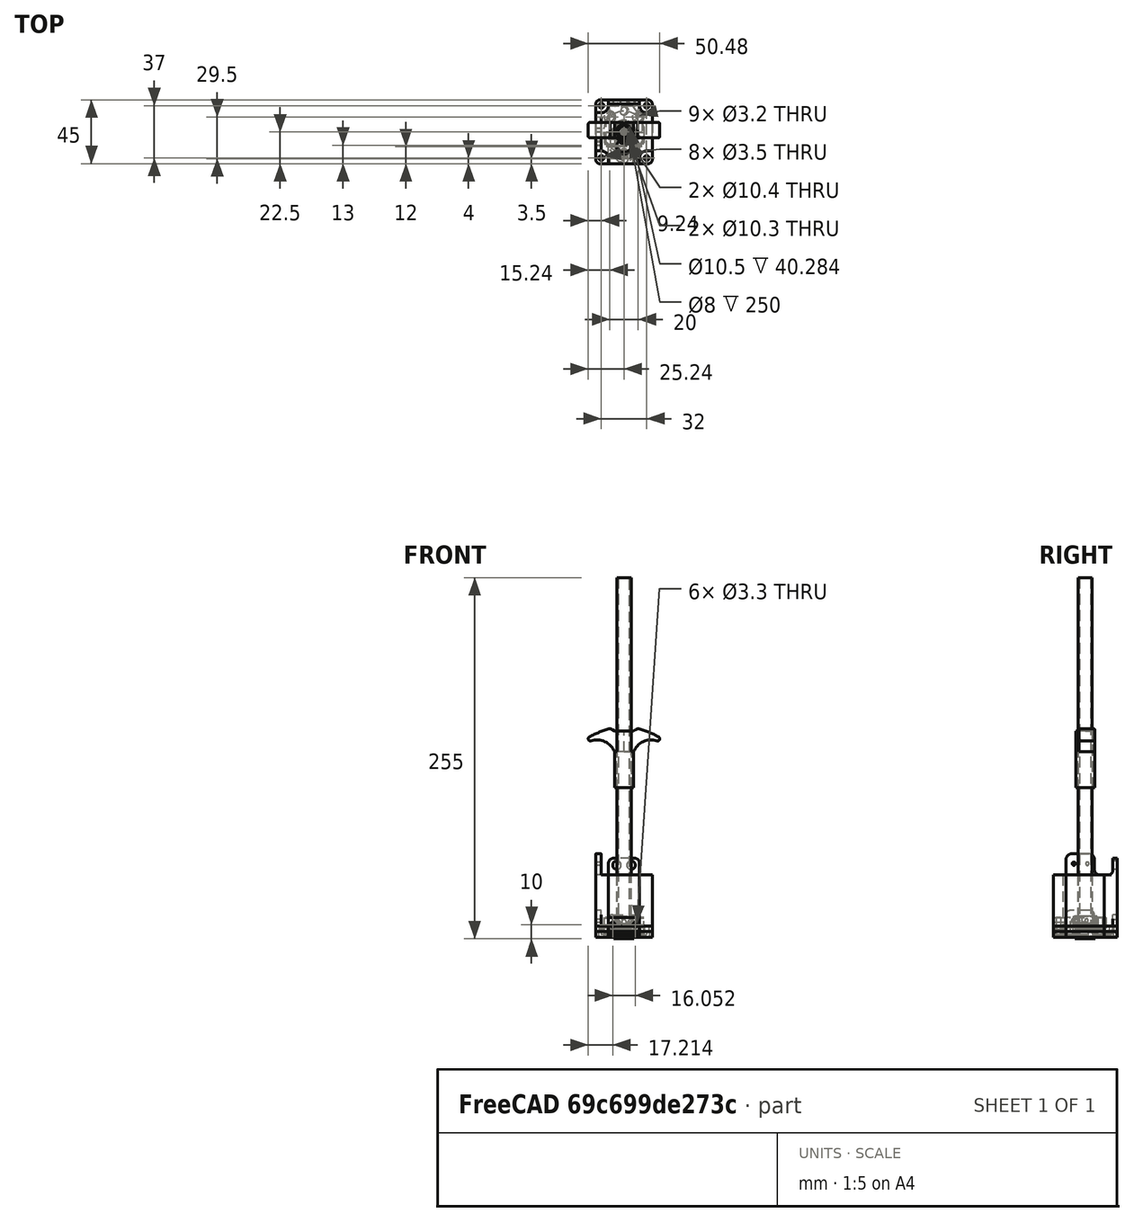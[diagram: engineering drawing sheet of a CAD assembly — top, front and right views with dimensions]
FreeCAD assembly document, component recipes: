
FREECAD ASSEMBLY — COMPONENT RECIPES ("AltGearHandle")

This assembly document has 9 components, labeled P0..P8 below (a component is one placed body or linked part). 9 of them carry a construction recipe — the FreeCAD feature program that regenerates the part from scratch, quoted from this document or its linked companion documents; the rest are supplied as boundary geometry only. No exploded tour is included for this assembly.
COMPONENT P0 — recipe-attached ("Handle001", modeled in this document).
Construction recipe (the document's own serialized feature program — sketch geometry with constraints, then the solid features built on it; lengths are millimeters unless a unit is written):

FEATURE [Sketcher::SketchObject] Sketch002  label="mastersketch"
  ArcFitTolerance = 0
  AttachmentSupport = -> [XZ_Plane001]
  FullyConstrained = false
  MakeInternals = false
  MapMode = 5
  Placement = pos=(0,0,0) rot=(1,0,0;1.5708rad)
  sketch-geometry (21):
    g0: LineSegment StartX=-5 StartY=101.6 StartZ=0 EndX=5 EndY=101.6 EndZ=0
    g1: LineSegment StartX=5 StartY=101.6 StartZ=0 EndX=5 EndY=-60 EndZ=0
    g2: LineSegment StartX=5 StartY=-60 StartZ=0 EndX=-5 EndY=-60 EndZ=0
    g3: LineSegment StartX=-5 StartY=-60 StartZ=0 EndX=-5 EndY=101.6 EndZ=0
    g4: LineSegment [constr] StartX=-25.4 StartY=0 StartZ=0 EndX=-25.4 EndY=147.32 EndZ=0
    g5: LineSegment [constr] StartX=25.4 StartY=0 StartZ=0 EndX=25.4 EndY=147.32 EndZ=0
    g6: LineSegment StartX=-6.70052 StartY=141.884 StartZ=0 EndX=6.70052 EndY=141.884 EndZ=0
    g7: LineSegment StartX=6.70052 StartY=141.884 StartZ=0 EndX=6.70052 EndY=101.6 EndZ=0
    g8: LineSegment StartX=6.70052 StartY=101.6 StartZ=0 EndX=-6.70052 EndY=101.6 EndZ=0
    g9: LineSegment StartX=-6.70052 StartY=101.6 StartZ=0 EndX=-6.70052 EndY=141.884 EndZ=0
    g10: ArcOfCircle CenterX=-19.1442 CenterY=122.136 CenterZ=0 NormalX=0 NormalY=0 NormalZ=1 AngleXU=0 Radius=13.3604 StartAngle=0.3726 EndAngle=1.90028
    g11: ArcOfCircle CenterX=-23.9395 CenterY=136.16 CenterZ=0 NormalX=0 NormalY=0 NormalZ=1 AngleXU=0 Radius=1.4605 StartAngle=1.94929 EndAngle=5.04187
    g12: LineSegment StartX=-24.4792 StartY=137.517 StartZ=0 EndX=-9.6647 EndY=143.408 EndZ=0
    g13: LineSegment StartX=-9.6647 StartY=143.408 StartZ=0 EndX=-6.70052 EndY=141.884 EndZ=0
    g14: LineSegment StartX=-6.70052 StartY=141.884 StartZ=0 EndX=-6.70052 EndY=127 EndZ=0
    g15: LineSegment StartX=6.70052 StartY=128.917 StartZ=0 EndX=6.70052 EndY=141.884 EndZ=0
    g16: LineSegment StartX=6.70052 StartY=141.884 StartZ=0 EndX=9.6647 EndY=143.408 EndZ=0
    g17: LineSegment StartX=9.6647 StartY=143.408 StartZ=0 EndX=24.4792 EndY=137.517 EndZ=0
    g18: ArcOfCircle CenterX=23.9395 CenterY=136.16 CenterZ=0 NormalX=0 NormalY=0 NormalZ=1 AngleXU=0 Radius=1.4605 StartAngle=4.38291 EndAngle=7.47549
    g19: ArcOfCircle CenterX=19.1442 CenterY=122.136 CenterZ=0 NormalX=0 NormalY=0 NormalZ=1 AngleXU=0 Radius=13.3604 StartAngle=1.24132 EndAngle=2.76899
    g20: LineSegment StartX=6.70052 StartY=127 StartZ=0 EndX=6.70052 EndY=141.884 EndZ=0
  constraints (58):
    c: Coincident(g0,g1)
    c: Coincident(g1,g2)
    c: Coincident(g2,g3)
    c: Coincident(g3,g0)
    c: Horizontal(g0)
    c: Vertical(g1)
    c: Vertical(g3)
    c: Symmetric(g2,g1,g-2)
    c: DistanceX(g2,g2) = 10
    c: DistanceY(g0) = 101.6
    c: DistanceY(g1) = -60
    c: PointOnObject(g4,g-1)
    c: Vertical(g4)
    c: PointOnObject(g5,g-1)
    c: Vertical(g5)
    c: Symmetric(g5,g4,g-2)
    c: DistanceX(g4,g5) = 50.8
    c: DistanceY(g0,g5) = 45.72
    c: Coincident(g6,g7)
    c: Coincident(g7,g8)
    c: Coincident(g8,g9)
    c: Coincident(g9,g6)
    c: Horizontal(g6)
    c: Vertical(g7)
    c: Vertical(g9)
    c: Horizontal(g0,g7)
    c: Symmetric(g8,g7,g-2)
    c: DistanceX(g8,g8) = 13.401
    c: DistanceY(g6,g5) = 5.4356
    c: PointOnObject(g10,g9)
    c: Tangent(g10,g11) = 1.5708
    c: Tangent(g11,g12) = 1.5708
    c: Coincident(g12,g13)
    c: Coincident(g13,g14)
    c: Coincident(g14,g10)
    c: PointOnObject(g15,g7)
    c: PointOnObject(g15,g7)
    c: Coincident(g15,g16)
    c: Coincident(g16,g17)
    c: Tangent(g17,g18) = 1.5708
    c: Tangent(g18,g19) = 1.5708
    c: PointOnObject(g19,g7)
    c: Coincident(g20,g19)
    c: Coincident(g20,g15)
    c: Horizontal(g19,g10)
    c: Equal(g10,g19)
    c: Equal(g18,g11)
    c: Tangent(g18,g5)
    c: Symmetric(g18,g11,g-2)
    c: Horizontal(g13,g15)
    c: Symmetric(g16,g12,g-2)
    c: Radius(g19) = 13.3604
    c: Radius(g18) = 1.4605
    c: DistanceY(g8,g10) = 25.4
    c: DistanceY(g6,g16) = 1.524
    c: Coincident(g13,g6)
    c: DistanceX(g12,g16) = 19.3294
    c: DistanceY(g10,g11) = 9.16
FEATURE [Sketcher::SketchObject] Sketch004
  ArcFitTolerance = 0
  AttachmentOffset = pos=(0,0,-6.7) rot=(0,0,1;0rad)
  AttachmentSupport = -> [XZ_Plane001]
  ExternalGeometry = -> [Sketch002]
  FullyConstrained = true
  MakeInternals = false
  MapMode = 5
  Placement = pos=(0,6.7,-1.5e-15) rot=(1,0,0;1.5708rad)
  sketch-geometry (7):
    g0: LineSegment StartX=-6.70052 StartY=141.884 StartZ=0 EndX=-9.6647 EndY=143.408 EndZ=0
    g1: ArcOfCircle CenterX=-19.1442 CenterY=122.136 CenterZ=0 NormalX=0 NormalY=0 NormalZ=1 AngleXU=0 Radius=13.3604 StartAngle=0.3726 EndAngle=1.8879
    g2: LineSegment StartX=-6.70052 StartY=141.884 StartZ=0 EndX=0 EndY=141.884 EndZ=0
    g3: LineSegment StartX=0 StartY=141.884 StartZ=0 EndX=0 EndY=127 EndZ=0
    g4: LineSegment StartX=0 StartY=127 StartZ=0 EndX=-6.70052 EndY=127 EndZ=0
    g5: ArcOfCircle CenterX=6.31595 CenterY=81.6504 CenterZ=0 NormalX=0 NormalY=0 NormalZ=1 AngleXU=0 Radius=63.7921 StartAngle=1.824 EndAngle=2.07458
    g6: ArcOfCircle CenterX=-23.7689 CenterY=136.229 CenterZ=0 NormalX=0 NormalY=0 NormalZ=1 AngleXU=0 Radius=1.47134 StartAngle=2.07458 EndAngle=5.02949
  constraints (18):
    c: Coincident(g1,g-4)
    c: Coincident(g0,g-6)
    c: Parallel(g-6,g0)
    c: Coincident(g1,g-4)
    c: Coincident(g0,g2)
    c: Horizontal(g2)
    c: Coincident(g2,g3)
    c: Vertical(g3)
    c: Coincident(g3,g4)
    c: Coincident(g4,g1)
    c: Horizontal(g4)
    c: Horizontal(g0,g-6)
    c: PointOnObject(g2,g-2)
    c: Coincident(g5,g0)
    c: Radius(g5) = 63.7921
    c: Tangent(g6,g5) = -1.5708
    c: Tangent(g6,g1) = 1.5708
    c: Coincident(g-5,g5)
FEATURE [PartDesign::Pad] Pad001  label="gripBase1"
  Direction = (0,-1,2e-16)
  Length = 11
  Length2 = 10
  Placement = pos=(0,0,0) rot=(1,0,0;1.5708rad)
  Profile = -> Sketch004
  ReferenceAxis = -> Sketch004 [N_Axis]
  Suppressed = false
  Type = 0
FEATURE [PartDesign::Mirrored] Mirrored
  BaseFeature = -> Pad001
  MirrorPlane = -> Sketch004 [V_Axis]
  Originals = -> [Pad001]
  Placement = pos=(0,0,0) rot=(1,0,0;1.5708rad)
  Suppressed = false
  TransformMode = 0
FEATURE [PartDesign::Fillet] Fillet001  label="Grip"
  Base = -> Mirrored [Edge25,Edge29,Edge16,Edge11]
  BaseFeature = -> Mirrored
  Placement = pos=(0,0,0) rot=(1,0,0;1.5708rad)
  Radius = 1.2
  SupportTransform = false
  Suppressed = false
  UseAllEdges = false
FEATURE [Sketcher::SketchObject] Sketch005
  ArcFitTolerance = 0
  AttachmentSupport = -> [XZ_Plane001]
  ExternalGeometry = -> [Sketch002]
  FullyConstrained = true
  MakeInternals = false
  MapMode = 5
  Placement = pos=(0,0,0) rot=(1,0,0;1.5708rad)
  sketch-geometry (4):
    g0: LineSegment StartX=-6.70052 StartY=141.884 StartZ=0 EndX=0 EndY=141.884 EndZ=0
    g1: LineSegment StartX=0 StartY=141.884 StartZ=0 EndX=0 EndY=101.6 EndZ=0
    g2: LineSegment StartX=0 StartY=101.6 StartZ=0 EndX=-6.70052 EndY=101.6 EndZ=0
    g3: LineSegment StartX=-6.70052 StartY=101.6 StartZ=0 EndX=-6.70052 EndY=141.884 EndZ=0
  constraints (11):
    c: Coincident(g0,g1)
    c: Coincident(g1,g2)
    c: Coincident(g2,g3)
    c: Coincident(g3,g0)
    c: Horizontal(g0)
    c: Horizontal(g2)
    c: Vertical(g1)
    c: Vertical(g3)
    c: Coincident(g0,g-3)
    c: PointOnObject(g1,g-2)
    c: Horizontal(g-3,g1)
FEATURE [PartDesign::Revolution] Revolution
  Angle = 360
  Angle2 = 60
  Axis = (0,2e-16,1)
  Base = (0,0,0)
  BaseFeature = -> Fillet001
  Placement = pos=(0,0,0) rot=(1,0,0;1.5708rad)
  Profile = -> Sketch005
  ReferenceAxis = -> Sketch005 [V_Axis]
  Suppressed = false
  Type = 0
FEATURE [Sketcher::SketchObject] Sketch006
  ArcFitTolerance = 0
  AttachmentSupport = -> [XY_Plane001]
  ExternalGeometry = -> [Sketch002]
  FullyConstrained = true
  MakeInternals = false
  MapMode = 5
  sketch-geometry (1):
    g0: Circle CenterX=0 CenterY=0 CenterZ=0 NormalX=0 NormalY=0 NormalZ=1 AngleXU=0 Radius=5.25
  constraints (2):
    c: Coincident(g0,g-1)
    c: Diameter(g0) = 10.5
FEATURE [PartDesign::Pocket] Pocket
  BaseFeature = -> Revolution
  Direction = (0,0,-1)
  Length = 5
  Length2 = 5
  Midplane = true
  Placement = pos=(0,0,0) rot=(1,0,0;1.5708rad)
  Profile = -> Sketch006
  ReferenceAxis = -> Sketch006 [N_Axis]
  Suppressed = false
  Type = 1
FEATURE [PartDesign::Plane] DatumPlane
  AttachmentSupport = -> [Pocket]
  Length = 60.0479
  MapMode = 45
  Placement = pos=(0,6.70021,141.884) rot=(0,0,1;1.5708rad)
  ResizeMode = 0
  Width = 60.5283
FEATURE [PartDesign::Plane] DatumPlane001
  AttachmentSupport = -> [Pocket]
  Length = 193.249
  MapMode = 45
  Placement = pos=(-24.6781,1.2,135.833) rot=(0.548172,0,0.836366;3.14159rad)
  ResizeMode = 0
  Width = 68.6849
FEATURE [PartDesign::Body] Body001  label="Handle"
  AllowCompound = false
  Group = -> [Sketch002,Sketch004,Pad001,Mirrored,Fillet001,Sketch005,Revolution,Sketch006,Pocket,DatumPlane,DatumPlane001]
  Origin = -> Origin001
  Tip = -> Pocket
COMPONENT P1 — recipe-attached ("Rod001", modeled in this document).
Construction recipe (the document's own serialized feature program — sketch geometry with constraints, then the solid features built on it; lengths are millimeters unless a unit is written):

FEATURE [Sketcher::SketchObject] Sketch043
  ArcFitTolerance = 1e-06
  AttachmentSupport = -> [XY_Plane012]
  FullyConstrained = true
  MakeInternals = false
  MapMode = 5
  sketch-geometry (2):
    g0: Circle CenterX=0 CenterY=0 CenterZ=0 NormalX=0 NormalY=0 NormalZ=1 AngleXU=0 Radius=5
    g1: Circle CenterX=0 CenterY=0 CenterZ=0 NormalX=0 NormalY=0 NormalZ=1 AngleXU=0 Radius=4
  constraints (4):
    c: Coincident(g0,g-1)
    c: Coincident(g1,g0)
    c: Diameter(g0) = 10
    c: Diameter(g1) = 8
FEATURE [PartDesign::Pad] Pad017
  Direction = (0,0,1)
  Length = 250
  Length2 = 10
  Profile = -> Sketch043
  ReferenceAxis = -> Sketch043 [N_Axis]
  Suppressed = false
  Type = 0
FEATURE [PartDesign::Body] Body012  label="Rod"
  AllowCompound = false
  Group = -> [Sketch043,Pad017]
  Origin = -> Origin012
  Tip = -> Pad017
COMPONENT P2 — recipe-attached ("SlidingBodyBottom001", modeled in this document).
Construction recipe (the document's own serialized feature program — sketch geometry with constraints, then the solid features built on it; lengths are millimeters unless a unit is written):

FEATURE [Sketcher::SketchObject] Sketch029
  ArcFitTolerance = 1e-06
  AttachmentSupport = -> [XY_Plane009]
  FullyConstrained = true
  MakeInternals = false
  MapMode = 5
  sketch-geometry (25):
    g0: LineSegment StartX=-20 StartY=13.5 StartZ=0 EndX=-20 EndY=-13.5 EndZ=0
    g1: LineSegment StartX=-11 StartY=-22.5 StartZ=0 EndX=11 EndY=-22.5 EndZ=0
    g2: LineSegment StartX=11 StartY=22.5 StartZ=0 EndX=-11 EndY=22.5 EndZ=0
    g3: LineSegment [constr] StartX=-16 StartY=18.5 StartZ=0 EndX=-16 EndY=-18.5 EndZ=0
    g4: LineSegment [constr] StartX=-16 StartY=-18.5 StartZ=0 EndX=16 EndY=-18.5 EndZ=0
    g5: LineSegment [constr] StartX=16 StartY=-18.5 StartZ=0 EndX=16 EndY=18.5 EndZ=0
    g6: LineSegment [constr] StartX=16 StartY=18.5 StartZ=0 EndX=-16 EndY=18.5 EndZ=0
    g7: Circle CenterX=0 CenterY=-9.5 CenterZ=0 NormalX=0 NormalY=0 NormalZ=1 AngleXU=0 Radius=5.15
    g8: Circle CenterX=0 CenterY=-19 CenterZ=0 NormalX=0 NormalY=0 NormalZ=1 AngleXU=0 Radius=1.6
    g9: Circle [constr] CenterX=0 CenterY=-19 CenterZ=0 NormalX=0 NormalY=0 NormalZ=1 AngleXU=0 Radius=3.5
    g10: Circle CenterX=-10 CenterY=10.5 CenterZ=0 NormalX=0 NormalY=0 NormalZ=1 AngleXU=0 Radius=1.6
    g11: Circle CenterX=10 CenterY=10.5 CenterZ=0 NormalX=0 NormalY=0 NormalZ=1 AngleXU=0 Radius=1.6
    g12: ArcOfCircle CenterX=-16 CenterY=-18.5 CenterZ=0 NormalX=0 NormalY=0 NormalZ=1 AngleXU=0 Radius=5 StartAngle=4e-16 EndAngle=1.5708
    g13: LineSegment StartX=-11 StartY=-18.5 StartZ=0 EndX=-11 EndY=-22.5 EndZ=0
    g14: LineSegment StartX=-16 StartY=-13.5 StartZ=0 EndX=-20 EndY=-13.5 EndZ=0
    g15: LineSegment StartX=11 StartY=-22.5 StartZ=0 EndX=11 EndY=-18.5 EndZ=0
    g16: ArcOfCircle CenterX=16 CenterY=-18.5 CenterZ=0 NormalX=0 NormalY=0 NormalZ=1 AngleXU=0 Radius=5 StartAngle=1.5708 EndAngle=3.14159
    g17: LineSegment StartX=16 StartY=-13.5 StartZ=0 EndX=20 EndY=-13.5 EndZ=0
    g18: ArcOfCircle CenterX=16 CenterY=18.5 CenterZ=0 NormalX=0 NormalY=0 NormalZ=1 AngleXU=0 Radius=5 StartAngle=3.14159 EndAngle=4.71239
    g19: ArcOfCircle CenterX=-16 CenterY=18.5 CenterZ=0 NormalX=0 NormalY=0 NormalZ=1 AngleXU=0 Radius=5 StartAngle=4.71239 EndAngle=6.28319
    g20: LineSegment StartX=-11 StartY=18.5 StartZ=0 EndX=-11 EndY=22.5 EndZ=0
    g21: LineSegment StartX=-16 StartY=13.5 StartZ=0 EndX=-20 EndY=13.5 EndZ=0
    g22: LineSegment StartX=11 StartY=18.5 StartZ=0 EndX=11 EndY=22.5 EndZ=0
    g23: LineSegment StartX=16 StartY=13.5 StartZ=0 EndX=20 EndY=13.5 EndZ=0
    g24: LineSegment StartX=20 StartY=13.5 StartZ=0 EndX=20 EndY=-13.5 EndZ=0
  constraints (68):
    c: Vertical(g0)
    c: Horizontal(g1)
    c: Horizontal(g2)
    c: Coincident(g3,g4)
    c: Coincident(g4,g5)
    c: Coincident(g5,g6)
    c: Coincident(g6,g3)
    c: Vertical(g3)
    c: Vertical(g5)
    c: Horizontal(g4)
    c: Horizontal(g6)
    c: PointOnObject(g7,g-2)
    c: Diameter(g7) = 10.3
    c: Symmetric(g4,g3,g-1)
    c: PointOnObject(g8,g-2)
    c: Diameter(g8) = 3.2
    c: Coincident(g9,g8)
    c: Diameter(g9) = 7
    c: Tangent(g9,g1)
    c: Equal(g11,g10)
    c: Equal(g10,g8)
    c: DistanceY(g11,g5) = 8
    c: Symmetric(g11,g10,g-2)
    c: DistanceX(g10,g11) = 20
    c: Coincident(g12,g3)
    c: PointOnObject(g12,g3)
    c: PointOnObject(g12,g4)
    c: Coincident(g13,g12)
    c: Vertical(g13)
    c: Coincident(g14,g12)
    c: Horizontal(g14)
    c: Radius(g12) = 5
    c: PointOnObject(g15,g4)
    c: Tangent(g15,g16) = 1.5708
    c: PointOnObject(g16,g5)
    c: Tangent(g16,g17) = 1.5708
    c: Coincident(g4,g16)
    c: Coincident(g18,g5)
    c: PointOnObject(g18,g5)
    c: PointOnObject(g18,g6)
    c: Coincident(g19,g3)
    c: PointOnObject(g19,g3)
    c: PointOnObject(g19,g6)
    c: Coincident(g20,g19)
    c: Vertical(g20)
    c: Coincident(g21,g19)
    c: Horizontal(g21)
    c: Coincident(g22,g18)
    c: Vertical(g22)
    c: Coincident(g23,g18)
    c: Horizontal(g23)
    c: Equal(g16,g19)
    c: Coincident(g2,g20)
    c: Coincident(g0,g21)
    c: Coincident(g2,g22)
    c: Coincident(g1,g15)
    c: Coincident(g1,g13)
    c: Coincident(g0,g14)
    c: DistanceX(g1,g1) = 22
    c: DistanceY(g0,g0) = 27
    c: Coincident(g24,g23)
    c: Coincident(g24,g17)
    c: Vertical(g24)
    c: DistanceX(g0,g17) = 40
    c: DistanceY(g1,g2) = 45
    c: Symmetric(g23,g0,g-2)
    c: Symmetric(g2,g1,g-1)
    c: DistanceY(g4,g7) = 9
FEATURE [PartDesign::Pad] Pad011  label="FrontPad004"
  Direction = (0,0,1)
  Length = 4
  Length2 = 10
  Profile = -> Sketch029
  ReferenceAxis = -> Sketch029 [N_Axis]
  Reversed = true
  Suppressed = false
  Type = 0
FEATURE [Sketcher::SketchObject] Sketch030
  ArcFitTolerance = 1e-06
  ExternalGeometry = -> [Pad011]
  FullyConstrained = false
  MakeInternals = false
  MapMode = 5
  sketch-geometry (9):
    g0: Circle [constr] CenterX=0 CenterY=-9.5 CenterZ=0 NormalX=0 NormalY=0 NormalZ=1 AngleXU=0 Radius=14.5
    g1: LineSegment StartX=-20 StartY=-13.5 StartZ=0 EndX=-16 EndY=-13.5 EndZ=0
    g2: LineSegment StartX=-16 StartY=-13.5 StartZ=0 EndX=-16 EndY=6.5 EndZ=0
    g3: LineSegment StartX=-16 StartY=6.5 StartZ=0 EndX=-20 EndY=6.5 EndZ=0
    g4: LineSegment StartX=-20 StartY=6.5 StartZ=0 EndX=-20 EndY=-13.5 EndZ=0
    g5: LineSegment [constr] StartX=-16 StartY=6.5 StartZ=0 EndX=-16 EndY=-13.5 EndZ=0
    g6: LineSegment [constr] StartX=-16 StartY=-13.5 StartZ=0 EndX=-10 EndY=-13.5 EndZ=0
    g7: LineSegment [constr] StartX=-10 StartY=-13.5 StartZ=0 EndX=-10 EndY=6.5 EndZ=0
    g8: LineSegment [constr] StartX=-10 StartY=6.5 StartZ=0 EndX=-16 EndY=6.5 EndZ=0
  constraints (23):
    c: Diameter(g0) = 29
    c: Coincident(g1,g2)
    c: Coincident(g2,g3)
    c: Coincident(g3,g4)
    c: Coincident(g4,g1)
    c: Horizontal(g1)
    c: Horizontal(g3)
    c: Vertical(g2)
    c: Vertical(g4)
    c: Coincident(g1,g-4)
    c: Coincident(g5,g6)
    c: Coincident(g6,g7)
    c: Coincident(g7,g8)
    c: Coincident(g8,g5)
    c: Vertical(g5)
    c: Vertical(g7)
    c: Horizontal(g6)
    c: Horizontal(g8)
    c: Coincident(g5,g2)
    c: Horizontal(g1,g6)
    c: DistanceX(g3,g3) = 4
    c: DistanceX(g8,g8) = 6
    c: DistanceY(g4,g4) = 20
FEATURE [PartDesign::Pad] Pad012  label="SwitchMountPad006"
  BaseFeature = -> Pad011
  Direction = (0,0,1)
  Length = 15
  Length2 = 10
  Profile = -> Sketch030
  ReferenceAxis = -> Sketch030 [N_Axis]
  Suppressed = false
  Type = 0
FEATURE [Sketcher::SketchObject] Sketch031
  ArcFitTolerance = 1e-06
  AttachmentSupport = -> [Pad012]
  ExternalGeometry = -> [Pad012]
  FullyConstrained = true
  MakeInternals = false
  MapMode = 5
  Placement = pos=(-16,0,0) rot=(0.57735,0.57735,0.57735;2.0944rad)
  sketch-geometry (2):
    g0: Circle CenterX=-8.5 CenterY=8 CenterZ=0 NormalX=0 NormalY=0 NormalZ=1 AngleXU=0 Radius=1.15
    g1: Circle CenterX=1 CenterY=8 CenterZ=0 NormalX=0 NormalY=0 NormalZ=1 AngleXU=0 Radius=1.15
  constraints (6):
    c: Equal(g1,g0)
    c: Horizontal(g0,g1)
    c: DistanceX(g0,g1) = 9.5
    c: Diameter(g1) = 2.3
    c: DistanceX(g-3,g0) = 5
    c: DistanceY(g0,g-3) = 7
FEATURE [PartDesign::Pocket] Pocket011
  BaseFeature = -> Pad012
  Direction = (-1,0,0)
  Length = 5
  Length2 = 5
  Midplane = true
  Profile = -> Sketch031
  ReferenceAxis = -> Sketch031 [N_Axis]
  Suppressed = false
  Type = 1
FEATURE [Sketcher::SketchObject] Sketch035
  ArcFitTolerance = 1e-06
  AttachmentSupport = -> [Pocket011]
  ExternalGeometry = -> [Pocket011]
  FullyConstrained = true
  MakeInternals = false
  MapMode = 5
  sketch-geometry (4):
    g0: LineSegment StartX=-11 StartY=22.5 StartZ=0 EndX=-11 EndY=19.5 EndZ=0
    g1: LineSegment StartX=-11 StartY=19.5 StartZ=0 EndX=11 EndY=19.5 EndZ=0
    g2: LineSegment StartX=11 StartY=19.5 StartZ=0 EndX=11 EndY=22.5 EndZ=0
    g3: LineSegment StartX=11 StartY=22.5 StartZ=0 EndX=-11 EndY=22.5 EndZ=0
  constraints (10):
    c: Coincident(g0,g1)
    c: Coincident(g1,g2)
    c: Coincident(g2,g3)
    c: Coincident(g3,g0)
    c: Vertical(g0)
    c: Vertical(g2)
    c: Horizontal(g1)
    c: Coincident(g0,g-3)
    c: Coincident(g2,g-3)
    c: DistanceY(g0,g0) = 3
FEATURE [PartDesign::Pad] Pad013
  BaseFeature = -> Pocket011
  Direction = (0,0,1)
  Length = 12
  Length2 = 10
  Profile = -> Sketch035
  ReferenceAxis = -> Sketch035 [N_Axis]
  Suppressed = false
  Type = 0
FEATURE [Sketcher::SketchObject] Sketch036
  ArcFitTolerance = 1e-06
  AttachmentSupport = -> [XZ_Plane009]
  ExternalGeometry = -> [Pad013]
  FullyConstrained = true
  MakeInternals = false
  MapMode = 5
  Placement = pos=(0,0,0) rot=(1,0,0;1.5708rad)
  sketch-geometry (2):
    g0: Circle CenterX=-5 CenterY=6 CenterZ=0 NormalX=0 NormalY=0 NormalZ=1 AngleXU=0 Radius=2.5
    g1: Circle CenterX=5 CenterY=6 CenterZ=0 NormalX=0 NormalY=0 NormalZ=1 AngleXU=0 Radius=2.5
  constraints (5):
    c: Diameter(g1) = 5
    c: Equal(g1,g0)
    c: Symmetric(g1,g0,g-2)
    c: DistanceY(g0,g-3) = 6
    c: DistanceX(g0,g1) = 10
FEATURE [PartDesign::Pocket] Pocket012
  BaseFeature = -> Pad013
  Direction = (0,1,-2e-16)
  Length = 5
  Length2 = 5
  Profile = -> Sketch036
  ReferenceAxis = -> Sketch036 [N_Axis]
  Suppressed = false
  Type = 1
FEATURE [PartDesign::Fillet] Fillet006
  Base = -> Pocket012 [Edge85,Edge77,Edge84,Edge88]
  BaseFeature = -> Pocket012
  Radius = 3
  SupportTransform = false
  Suppressed = false
  UseAllEdges = false
FEATURE [PartDesign::Fillet] Fillet007
  Base = -> Fillet006 [Edge31,Edge11]
  BaseFeature = -> Fillet006
  Radius = 3
  SupportTransform = false
  Suppressed = false
  UseAllEdges = false
FEATURE [PartDesign::Body] Body009  label="SlidingBodyBottom"
  AllowCompound = false
  Group = -> [Sketch029,Pad011,Sketch030,Pad012,Sketch031,Pocket011,Sketch035,Pad013,Sketch036,Pocket012,Fillet006,Fillet007]
  Origin = -> Origin009
  Tip = -> Fillet007
COMPONENT P3 — recipe-attached ("SlidingBodyBrakeBase001", modeled in this document).
Construction recipe (the document's own serialized feature program — sketch geometry with constraints, then the solid features built on it; lengths are millimeters unless a unit is written):

FEATURE [Part::Part2DObjectPython] Clone2D  label="Sketch029 (2D)"  # Draft 2D object (typed FeaturePython)
  Fuse = false
  Objects = -> [Sketch029]
  Scale = (1,1,1)
FEATURE [Sketcher::SketchObject] Sketch037
  ArcFitTolerance = 1e-06
  AttachmentSupport = -> [XY_Plane010]
  ExternalGeometry = -> [Clone2D]
  FullyConstrained = true
  MakeInternals = false
  MapMode = 5
  sketch-geometry (14):
    g0: ArcOfCircle CenterX=-16 CenterY=18.5 CenterZ=0 NormalX=0 NormalY=0 NormalZ=1 AngleXU=0 Radius=5 StartAngle=4.71239 EndAngle=6.28319
    g1: ArcOfCircle CenterX=16 CenterY=18.5 CenterZ=0 NormalX=0 NormalY=0 NormalZ=1 AngleXU=0 Radius=5 StartAngle=3.14159 EndAngle=4.71239
    g2: ArcOfCircle CenterX=16 CenterY=-18.5 CenterZ=0 NormalX=0 NormalY=0 NormalZ=1 AngleXU=0 Radius=5 StartAngle=1.5708 EndAngle=3.14159
    g3: ArcOfCircle CenterX=-16 CenterY=-18.5 CenterZ=0 NormalX=0 NormalY=0 NormalZ=1 AngleXU=0 Radius=5 StartAngle=8e-16 EndAngle=1.5708
    g4: LineSegment StartX=-16 StartY=13.5 StartZ=0 EndX=-16 EndY=-13.5 EndZ=0
    g5: LineSegment StartX=16 StartY=-13.5 StartZ=0 EndX=16 EndY=13.5 EndZ=0
    g6: LineSegment StartX=-11 StartY=18.5 StartZ=0 EndX=11 EndY=18.5 EndZ=0
    g7: LineSegment StartX=-11 StartY=-18.5 StartZ=0 EndX=-11 EndY=-22.5 EndZ=0
    g8: LineSegment StartX=-11 StartY=-22.5 StartZ=0 EndX=11 EndY=-22.5 EndZ=0
    g9: LineSegment StartX=11 StartY=-22.5 StartZ=0 EndX=11 EndY=-18.5 EndZ=0
    g10: Circle CenterX=-10 CenterY=10.5 CenterZ=0 NormalX=0 NormalY=0 NormalZ=1 AngleXU=0 Radius=1.6
    g11: Circle CenterX=10 CenterY=10.5 CenterZ=0 NormalX=0 NormalY=0 NormalZ=1 AngleXU=0 Radius=1.6
    g12: Circle CenterX=0 CenterY=-9.5 CenterZ=0 NormalX=0 NormalY=0 NormalZ=1 AngleXU=0 Radius=5.65
    g13: Circle CenterX=0 CenterY=-19 CenterZ=0 NormalX=0 NormalY=0 NormalZ=1 AngleXU=0 Radius=1.6
  constraints (32):
    c: Coincident(g0,g-3)
    c: Coincident(g0,g-3)
    c: Coincident(g1,g-10)
    c: Coincident(g1,g-10)
    c: Coincident(g1,g-10)
    c: Coincident(g2,g-9)
    c: Coincident(g2,g-9)
    c: Coincident(g3,g-8)
    c: Coincident(g3,g-8)
    c: Vertical(g3,g0)
    c: Horizontal(g0,g0)
    c: Horizontal(g2,g2)
    c: Coincident(g4,g0)
    c: Coincident(g4,g3)
    c: Coincident(g5,g2)
    c: Coincident(g5,g1)
    c: Coincident(g6,g0)
    c: Coincident(g6,g1)
    c: Tangent(g3,g7) = 1.5708
    c: Coincident(g7,g8)
    c: Coincident(g8,g-11)
    c: Horizontal(g8)
    c: Coincident(g8,g9)
    c: Coincident(g9,g2)
    c: Coincident(g10,g-4)
    c: Coincident(g11,g-5)
    c: Coincident(g12,g-7)
    c: Coincident(g13,g-6)
    c: Equal(g13,g11)
    c: Equal(g11,g10)
    c: Equal(g10,g-4)
    c: Distance(g12,g-7) = 0.5
FEATURE [PartDesign::Pad] Pad014  label="BasePad014"
  Direction = (0,0,1)
  Length = 2
  Length2 = 10
  Profile = -> Sketch037
  ReferenceAxis = -> Sketch037 [N_Axis]
  Reversed = true
  Suppressed = false
  Type = 0
FEATURE [Sketcher::SketchObject] Sketch038
  ArcFitTolerance = 1e-06
  AttachmentSupport = -> [XY_Plane010]
  ExternalGeometry = -> [Clone2D]
  FullyConstrained = true
  MakeInternals = false
  MapMode = 5
  sketch-geometry (11):
    g0: ArcOfCircle CenterX=0 CenterY=-9.5 CenterZ=0 NormalX=0 NormalY=0 NormalZ=1 AngleXU=0 Radius=5.15 StartAngle=3.33701 EndAngle=6.08777
    g1: LineSegment StartX=5.05198 StartY=-10.5 StartZ=0 EndX=11 EndY=-10.5 EndZ=0
    g2: LineSegment StartX=11 StartY=-10.5 StartZ=0 EndX=11 EndY=-22.5 EndZ=0
    g3: LineSegment StartX=11 StartY=-22.5 StartZ=0 EndX=-11 EndY=-22.5 EndZ=0
    g4: LineSegment StartX=-11 StartY=-22.5 StartZ=0 EndX=-11 EndY=-10.5 EndZ=0
    g5: LineSegment StartX=-11 StartY=-10.5 StartZ=0 EndX=-5.05198 EndY=-10.5 EndZ=0
    g6: Circle CenterX=0 CenterY=-19 CenterZ=0 NormalX=0 NormalY=0 NormalZ=1 AngleXU=0 Radius=1.6
    g7: Circle CenterX=-10 CenterY=10.5 CenterZ=0 NormalX=0 NormalY=0 NormalZ=1 AngleXU=0 Radius=1.6
    g8: Circle CenterX=10 CenterY=10.5 CenterZ=0 NormalX=0 NormalY=0 NormalZ=1 AngleXU=0 Radius=1.6
    g9: Circle CenterX=-10 CenterY=10.5 CenterZ=0 NormalX=0 NormalY=0 NormalZ=1 AngleXU=0 Radius=4.1
    g10: Circle CenterX=10 CenterY=10.5 CenterZ=0 NormalX=0 NormalY=0 NormalZ=1 AngleXU=0 Radius=4.1
  constraints (26):
    c: Coincident(g0,g-3)
    c: Equal(g0,g-3)
    c: Horizontal(g0,g0)
    c: DistanceY(g0,g0) = 1
    c: Coincident(g0,g1)
    c: Horizontal(g1)
    c: Coincident(g1,g2)
    c: Coincident(g2,g-4)
    c: Vertical(g2)
    c: Coincident(g2,g3)
    c: Coincident(g3,g-4)
    c: Coincident(g3,g4)
    c: Vertical(g4)
    c: Coincident(g4,g5)
    c: Coincident(g5,g0)
    c: Horizontal(g5)
    c: Coincident(g6,g-5)
    c: Equal(g6,g-5)
    c: Coincident(g7,g-6)
    c: Coincident(g8,g-7)
    c: Equal(g8,g7)
    c: Equal(g7,g6)
    c: Coincident(g9,g7)
    c: Coincident(g10,g8)
    c: Equal(g10,g9)
    c: Distance(g9,g7) = 2.5
FEATURE [PartDesign::Pad] Pad015  label="BrakeMainPad015"
  BaseFeature = -> Pad014
  Direction = (0,0,1)
  Length = 10
  Length2 = 10
  Profile = -> Sketch038
  ReferenceAxis = -> Sketch038 [N_Axis]
  Suppressed = false
  Type = 0
FEATURE [Sketcher::SketchObject] Sketch039
  ArcFitTolerance = 1e-06
  AttachmentSupport = -> [XZ_Plane010]
  ExternalGeometry = -> [Pad015]
  FullyConstrained = true
  MakeInternals = false
  MapMode = 5
  Placement = pos=(0,0,0) rot=(1,0,0;1.5708rad)
  sketch-geometry (5):
    g0: Circle CenterX=-8.02599 CenterY=5 CenterZ=0 NormalX=0 NormalY=0 NormalZ=1 AngleXU=0 Radius=1.65
    g1: Circle CenterX=8.02599 CenterY=5 CenterZ=0 NormalX=0 NormalY=0 NormalZ=1 AngleXU=0 Radius=1.65
    g2: LineSegment [constr] StartX=-11 StartY=5 StartZ=0 EndX=-5.05198 EndY=5 EndZ=0
    g3: LineSegment [constr] StartX=-11 StartY=10 StartZ=0 EndX=-5.05198 EndY=10 EndZ=0
    g4: LineSegment [constr] StartX=-8.02599 StartY=10 StartZ=0 EndX=-8.02599 EndY=5 EndZ=0
  constraints (11):
    c: Symmetric(g1,g0,g-2)
    c: Symmetric(g-3,g-3,g2)
    c: Symmetric(g-4,g-4,g2)
    c: PointOnObject(g0,g2)
    c: Coincident(g3,g-3)
    c: Coincident(g3,g-4)
    c: Symmetric(g3,g3,g4)
    c: Coincident(g4,g0)
    c: Vertical(g4)
    c: Equal(g0,g1)
    c: Diameter(g0) = 3.3
FEATURE [PartDesign::Pocket] Pocket013
  BaseFeature = -> Pad015
  Direction = (0,1,-2e-16)
  Length = 5
  Length2 = 5
  Profile = -> Sketch039
  ReferenceAxis = -> Sketch039 [N_Axis]
  Reversed = true
  Suppressed = false
  Type = 1
FEATURE [PartDesign::Body] Body010  label="SlidingBodyBrakeBase"
  AllowCompound = false
  Group = -> [Clone2D,Sketch037,Pad014,Sketch038,Pad015,Sketch039,Pocket013]
  Origin = -> Origin010
  Tip = -> Pocket013
COMPONENT P4 — recipe-attached ("SlidingBodyBrakePad001", modeled in this document).
Construction recipe (the document's own serialized feature program — sketch geometry with constraints, then the solid features built on it; lengths are millimeters unless a unit is written):

FEATURE [Part::Part2DObjectPython] Clone2D001  label="Sketch029 (2D)001"  # Draft 2D object (typed FeaturePython)
  Fuse = false
  Objects = -> [Sketch029]
  Scale = (1,1,1)
FEATURE [Sketcher::SketchObject] Sketch040
  ArcFitTolerance = 1e-06
  AttachmentSupport = -> [XY_Plane011]
  ExternalGeometry = -> [Clone2D001]
  FullyConstrained = true
  MakeInternals = false
  MapMode = 5
  sketch-geometry (6):
    g0: ArcOfCircle CenterX=0 CenterY=-9.5 CenterZ=0 NormalX=0 NormalY=0 NormalZ=1 AngleXU=0 Radius=5.15 StartAngle=0.195416 EndAngle=2.94618
    g1: LineSegment StartX=-14 StartY=-0.5 StartZ=0 EndX=-14 EndY=-8.5 EndZ=0
    g2: LineSegment StartX=-14 StartY=-8.5 StartZ=0 EndX=-5.05198 EndY=-8.5 EndZ=0
    g3: LineSegment StartX=-14 StartY=-0.5 StartZ=0 EndX=14 EndY=-0.5 EndZ=0
    g4: LineSegment StartX=14 StartY=-0.5 StartZ=0 EndX=14 EndY=-8.5 EndZ=0
    g5: LineSegment StartX=14 StartY=-8.5 StartZ=0 EndX=5.05198 EndY=-8.5 EndZ=0
  constraints (17):
    c: Coincident(g0,g-3)
    c: Horizontal(g0,g0)
    c: DistanceY(g0,g0) = 1
    c: Vertical(g1)
    c: Coincident(g1,g2)
    c: Coincident(g2,g0)
    c: Horizontal(g2)
    c: Coincident(g1,g3)
    c: Coincident(g3,g4)
    c: Vertical(g4)
    c: Coincident(g4,g5)
    c: Coincident(g5,g0)
    c: Horizontal(g5)
    c: Equal(g-3,g0)
    c: DistanceY(g4,g4) = 8
    c: Symmetric(g3,g1,g-2)
    c: DistanceX(g3,g3) = 28
FEATURE [PartDesign::Pad] Pad016
  Direction = (0,0,1)
  Length = 9.7
  Length2 = 10
  Profile = -> Sketch040
  ReferenceAxis = -> Sketch040 [N_Axis]
  Suppressed = false
  Type = 0
FEATURE [Sketcher::SketchObject] Sketch041
  ArcFitTolerance = 1e-06
  AttachmentSupport = -> [XZ_Plane011]
  ExternalGeometry = -> [Pad015]
  FullyConstrained = true
  MakeInternals = false
  MapMode = 5
  Placement = pos=(0,0,0) rot=(1,0,0;1.5708rad)
  sketch-geometry (5):
    g0: Circle CenterX=-8.02599 CenterY=5 CenterZ=0 NormalX=0 NormalY=0 NormalZ=1 AngleXU=0 Radius=1.65
    g1: Circle CenterX=8.02599 CenterY=5 CenterZ=0 NormalX=0 NormalY=0 NormalZ=1 AngleXU=0 Radius=1.65
    g2: LineSegment [constr] StartX=-11 StartY=5 StartZ=0 EndX=-5.05198 EndY=5 EndZ=0
    g3: LineSegment [constr] StartX=-11 StartY=10 StartZ=0 EndX=-5.05198 EndY=10 EndZ=0
    g4: LineSegment [constr] StartX=-8.02599 StartY=10 StartZ=0 EndX=-8.02599 EndY=5 EndZ=0
  constraints (11):
    c: Symmetric(g1,g0,g-2)
    c: Symmetric(g-3,g-3,g2)
    c: Symmetric(g-4,g-4,g2)
    c: PointOnObject(g0,g2)
    c: Coincident(g3,g-3)
    c: Coincident(g3,g-4)
    c: Symmetric(g3,g3,g4)
    c: Coincident(g4,g0)
    c: Vertical(g4)
    c: Equal(g0,g1)
    c: Diameter(g0) = 3.3
FEATURE [PartDesign::Pocket] Pocket014  label="ScrewHolePocket014"
  BaseFeature = -> Pad016
  Direction = (0,1,-2e-16)
  Length = 5
  Length2 = 5
  Midplane = true
  Profile = -> Sketch041
  ReferenceAxis = -> Sketch041 [N_Axis]
  Suppressed = false
  Type = 1
FEATURE [Sketcher::SketchObject] Sketch042
  ArcFitTolerance = 1e-06
  AttachmentSupport = -> [Pocket014]
  ExternalGeometry = -> [Pocket014]
  FullyConstrained = true
  MakeInternals = false
  MapMode = 5
  Placement = pos=(0,0,9.7) rot=(0,0,1;0rad)
  sketch-geometry (5):
    g0: LineSegment StartX=-10.926 StartY=-2.5 StartZ=0 EndX=-10.926 EndY=-5.2 EndZ=0
    g1: LineSegment StartX=-10.926 StartY=-5.2 StartZ=0 EndX=-5.12599 EndY=-5.2 EndZ=0
    g2: LineSegment StartX=-5.12599 StartY=-5.2 StartZ=0 EndX=-5.12599 EndY=-2.5 EndZ=0
    g3: LineSegment StartX=-5.12599 StartY=-2.5 StartZ=0 EndX=-10.926 EndY=-2.5 EndZ=0
    g4: LineSegment [constr] StartX=-8.02599 StartY=-8.5 StartZ=0 EndX=-8.02599 EndY=-5.2 EndZ=0
  constraints (14):
    c: Coincident(g0,g1)
    c: Coincident(g1,g2)
    c: Coincident(g2,g3)
    c: Coincident(g3,g0)
    c: Vertical(g0)
    c: Vertical(g2)
    c: Horizontal(g1)
    c: Horizontal(g3)
    c: DistanceX(g3,g3) = 5.8
    c: Symmetric(g-3,g-3,g4)
    c: PointOnObject(g4,g1)
    c: Symmetric(g0,g1,g4)
    c: DistanceY(g0,g0) = 2.7
    c: DistanceY(g0,g-4) = 2
FEATURE [PartDesign::Pocket] Pocket015
  BaseFeature = -> Pocket014
  Direction = (0,0,-1)
  Length = 8.3
  Length2 = 5
  Profile = -> Sketch042
  ReferenceAxis = -> Sketch042 [N_Axis]
  Suppressed = false
  Type = 0
FEATURE [PartDesign::Mirrored] Mirrored001
  BaseFeature = -> Pocket015
  MirrorPlane = -> Sketch042 [V_Axis]
  Originals = -> [Pocket015]
  Suppressed = false
  TransformMode = 0
FEATURE [PartDesign::Body] Body011  label="SlidingBodyBrakePad"
  AllowCompound = false
  Group = -> [Clone2D001,Sketch040,Pad016,Sketch041,Pocket014,Sketch042,Pocket015,Mirrored001]
  Origin = -> Origin011
  Tip = -> Mirrored001
COMPONENT P5 — recipe-attached ("SlidingBodyTop001", modeled in this document).
Construction recipe (the document's own serialized feature program — sketch geometry with constraints, then the solid features built on it; lengths are millimeters unless a unit is written):

FEATURE [Sketcher::SketchObject] Sketch023
  ArcFitTolerance = 1e-06
  AttachmentSupport = -> [XY_Plane008]
  FullyConstrained = true
  MakeInternals = false
  MapMode = 5
  sketch-geometry (17):
    g0: LineSegment StartX=-20 StartY=22.5 StartZ=0 EndX=-20 EndY=-22.5 EndZ=0
    g1: LineSegment StartX=-20 StartY=-22.5 StartZ=0 EndX=20 EndY=-22.5 EndZ=0
    g2: LineSegment StartX=20 StartY=-22.5 StartZ=0 EndX=20 EndY=22.5 EndZ=0
    g3: LineSegment StartX=20 StartY=22.5 StartZ=0 EndX=-20 EndY=22.5 EndZ=0
    g4: LineSegment [constr] StartX=-16 StartY=18.5 StartZ=0 EndX=-16 EndY=-18.5 EndZ=0
    g5: LineSegment [constr] StartX=-16 StartY=-18.5 StartZ=0 EndX=16 EndY=-18.5 EndZ=0
    g6: LineSegment [constr] StartX=16 StartY=-18.5 StartZ=0 EndX=16 EndY=18.5 EndZ=0
    g7: LineSegment [constr] StartX=16 StartY=18.5 StartZ=0 EndX=-16 EndY=18.5 EndZ=0
    g8: Circle CenterX=-16 CenterY=18.5 CenterZ=0 NormalX=0 NormalY=0 NormalZ=1 AngleXU=0 Radius=1.75
    g9: Circle CenterX=16 CenterY=18.5 CenterZ=0 NormalX=0 NormalY=0 NormalZ=1 AngleXU=0 Radius=1.75
    g10: Circle CenterX=16 CenterY=-18.5 CenterZ=0 NormalX=0 NormalY=0 NormalZ=1 AngleXU=0 Radius=1.75
    g11: Circle CenterX=-16 CenterY=-18.5 CenterZ=0 NormalX=0 NormalY=0 NormalZ=1 AngleXU=0 Radius=1.75
    g12: Circle CenterX=0 CenterY=-9.5 CenterZ=0 NormalX=0 NormalY=0 NormalZ=1 AngleXU=0 Radius=5.15
    g13: Circle CenterX=0 CenterY=-19 CenterZ=0 NormalX=0 NormalY=0 NormalZ=1 AngleXU=0 Radius=1.6
    g14: Circle [constr] CenterX=0 CenterY=-19 CenterZ=0 NormalX=0 NormalY=0 NormalZ=1 AngleXU=0 Radius=3.5
    g15: Circle CenterX=-10 CenterY=10.5 CenterZ=0 NormalX=0 NormalY=0 NormalZ=1 AngleXU=0 Radius=1.6
    g16: Circle CenterX=10 CenterY=10.5 CenterZ=0 NormalX=0 NormalY=0 NormalZ=1 AngleXU=0 Radius=1.6
  constraints (43):
    c: Coincident(g0,g1)
    c: Coincident(g1,g2)
    c: Coincident(g2,g3)
    c: Coincident(g3,g0)
    c: Vertical(g0)
    c: Vertical(g2)
    c: Horizontal(g1)
    c: Horizontal(g3)
    c: Symmetric(g0,g1,g-1)
    c: Coincident(g4,g5)
    c: Coincident(g5,g6)
    c: Coincident(g6,g7)
    c: Coincident(g7,g4)
    c: Vertical(g4)
    c: Vertical(g6)
    c: Horizontal(g5)
    c: Horizontal(g7)
    c: DistanceX(g0,g4) = 4
    c: DistanceY(g4,g0) = 4
    c: Coincident(g8,g4)
    c: Coincident(g9,g6)
    c: Coincident(g10,g5)
    c: Coincident(g11,g4)
    c: Equal(g8,g9)
    c: Equal(g9,g10)
    c: Equal(g10,g11)
    c: Diameter(g8) = 3.5
    c: PointOnObject(g12,g-2)
    c: Diameter(g12) = 10.3
    c: Symmetric(g5,g4,g-1)
    c: DistanceY(g2,g2) = 45
    c: DistanceX(g3,g3) = 40
    c: DistanceY(g1,g12) = 13
    c: PointOnObject(g13,g-2)
    c: Diameter(g13) = 3.2
    c: Coincident(g14,g13)
    c: Diameter(g14) = 7
    c: Tangent(g14,g1)
    c: Equal(g16,g15)
    c: Equal(g15,g13)
    c: DistanceY(g16,g6) = 8
    c: Symmetric(g16,g15,g-2)
    c: DistanceX(g15,g16) = 20
FEATURE [PartDesign::Pad] Pad007  label="FrontPad003"
  Direction = (0,0,1)
  Length = 4
  Length2 = 10
  Profile = -> Sketch023
  ReferenceAxis = -> Sketch023 [N_Axis]
  Suppressed = false
  Type = 0
FEATURE [PartDesign::Fillet] Fillet005
  Base = -> Pad007 [Edge8,Edge2,Edge1,Edge5]
  BaseFeature = -> Pad007
  Radius = 3
  SupportTransform = false
  Suppressed = false
  UseAllEdges = false
FEATURE [Sketcher::SketchObject] Sketch034
  ArcFitTolerance = 1e-06
  AttachmentSupport = -> [XY_Plane008]
  ExternalGeometry = -> [Pad007]
  FullyConstrained = true
  MakeInternals = false
  MapMode = 5
  sketch-geometry (3):
    g0: Circle CenterX=0 CenterY=-19 CenterZ=0 NormalX=0 NormalY=0 NormalZ=1 AngleXU=0 Radius=1.6
    g1: Circle CenterX=10 CenterY=10.5 CenterZ=0 NormalX=0 NormalY=0 NormalZ=1 AngleXU=0 Radius=1.6
    g2: Circle CenterX=-10 CenterY=10.5 CenterZ=0 NormalX=0 NormalY=0 NormalZ=1 AngleXU=0 Radius=1.6
  constraints (6):
    c: Coincident(g0,g-5)
    c: Equal(g0,g-5)
    c: Coincident(g1,g-4)
    c: Equal(g1,g-4)
    c: Coincident(g2,g-3)
    c: Equal(g2,g-3)
FEATURE [PartDesign::Hole] Hole001
  BaseFeature = -> Fillet005
  CustomThreadClearance = 0
  Depth = 25
  DepthType = 0
  Diameter = 3.4
  DrillForDepth = false
  DrillPoint = 1
  DrillPointAngle = 118
  HoleCutCountersinkAngle = 90
  HoleCutCustomValues = false
  HoleCutDepth = 0
  HoleCutDiameter = 6.2
  HoleCutType = 2
  ModelThread = false
  Profile = -> Sketch034
  Reversed = true
  Suppressed = false
  Tapered = false
  TaperedAngle = 90
  ThreadClass = 0
  ThreadDepth = 25
  ThreadDepthType = 0
  ThreadDirection = 0
  ThreadFit = 0
  ThreadSize = 9
  ThreadType = 1
  Threaded = false
  UseCustomThreadClearance = false
FEATURE [PartDesign::Body] Body008  label="SlidingBodyTop"
  AllowCompound = false
  Group = -> [Sketch023,Pad007,Fillet005,Sketch034,Hole001]
  Origin = -> Origin008
  Tip = -> Hole001
COMPONENT P6 — recipe-attached ("SlidingStop001", modeled in this document).
Construction recipe (the document's own serialized feature program — sketch geometry with constraints, then the solid features built on it; lengths are millimeters unless a unit is written):

FEATURE [Sketcher::SketchObject] Sketch018
  ArcFitTolerance = 1e-06
  AttachmentSupport = -> [XY_Plane006]
  FullyConstrained = true
  MakeInternals = false
  MapMode = 5
  sketch-geometry (2):
    g0: Circle CenterX=0 CenterY=0 CenterZ=0 NormalX=0 NormalY=0 NormalZ=1 AngleXU=0 Radius=7.2
    g1: Circle CenterX=0 CenterY=0 CenterZ=0 NormalX=0 NormalY=0 NormalZ=1 AngleXU=0 Radius=5.2
  constraints (4):
    c: Coincident(g0,g-1)
    c: Coincident(g1,g0)
    c: Diameter(g1) = 10.4
    c: Distance(g0,g1) = 2
FEATURE [PartDesign::Pad] Pad006
  Direction = (0,0,1)
  Length = 10
  Length2 = 10
  Midplane = true
  Profile = -> Sketch018
  ReferenceAxis = -> Sketch018 [N_Axis]
  Suppressed = false
  Type = 0
FEATURE [Sketcher::SketchObject] Sketch019
  ArcFitTolerance = 1e-06
  AttachmentSupport = -> [XZ_Plane006]
  FullyConstrained = true
  MakeInternals = false
  MapMode = 5
  Placement = pos=(0,0,0) rot=(1,0,0;1.5708rad)
  sketch-geometry (1):
    g0: Circle CenterX=0 CenterY=0 CenterZ=0 NormalX=0 NormalY=0 NormalZ=1 AngleXU=0 Radius=1.5
  constraints (2):
    c: Coincident(g0,g-1)
    c: Diameter(g0) = 3
FEATURE [PartDesign::Pocket] Pocket004
  BaseFeature = -> Pad006
  Direction = (0,1,-2e-16)
  Length = 5
  Length2 = 5
  Midplane = true
  Profile = -> Sketch019
  ReferenceAxis = -> Sketch019 [N_Axis]
  Suppressed = false
  Type = 1
FEATURE [PartDesign::Body] Body006  label="SlidingStop"
  AllowCompound = false
  Group = -> [Sketch018,Pad006,Sketch019,Pocket004]
  Origin = -> Origin006
  Tip = -> Pocket004
COMPONENT P7 — recipe-attached ("SwitchActuator001", modeled in this document).
Construction recipe (the document's own serialized feature program — sketch geometry with constraints, then the solid features built on it; lengths are millimeters unless a unit is written):

FEATURE [Sketcher::SketchObject] Sketch020
  ArcFitTolerance = 1e-06
  AttachmentSupport = -> [XZ_Plane007]
  FullyConstrained = true
  MakeInternals = false
  MapMode = 5
  Placement = pos=(0,0,0) rot=(1,0,0;1.5708rad)
  sketch-geometry (6):
    g0: LineSegment StartX=-14.5 StartY=0 StartZ=0 EndX=-14.5 EndY=3 EndZ=0
    g1: LineSegment StartX=-14.5 StartY=3 StartZ=0 EndX=-8.2 EndY=3 EndZ=0
    g2: LineSegment StartX=-8.2 StartY=3 StartZ=0 EndX=-8.2 EndY=11 EndZ=0
    g3: LineSegment StartX=-8.2 StartY=11 StartZ=0 EndX=-5.2 EndY=11 EndZ=0
    g4: LineSegment StartX=-5.2 StartY=11 StartZ=0 EndX=-5.2 EndY=0 EndZ=0
    g5: LineSegment StartX=-5.2 StartY=0 StartZ=0 EndX=-14.5 EndY=0 EndZ=0
  constraints (18):
    c: PointOnObject(g0,g-1)
    c: Vertical(g0)
    c: Coincident(g0,g1)
    c: Horizontal(g1)
    c: Coincident(g1,g2)
    c: Vertical(g2)
    c: Coincident(g2,g3)
    c: Horizontal(g3)
    c: Coincident(g3,g4)
    c: PointOnObject(g4,g-1)
    c: Vertical(g4)
    c: Coincident(g4,g5)
    c: Coincident(g5,g0)
    c: DistanceX(g4,g-1) = 5.2
    c: DistanceX(g3,g3) = 3
    c: DistanceX(g0,g-1) = 14.5
    c: DistanceY(g0,g0) = 3
    c: DistanceY(g2,g2) = 8
FEATURE [PartDesign::Revolution] Revolution004
  Angle = 360
  Angle2 = 60
  Axis = (0,2e-16,1)
  Base = (0,0,0)
  Placement = pos=(0,0,0) rot=(1,0,0;1.5708rad)
  Profile = -> Sketch020
  ReferenceAxis = -> Sketch020 [V_Axis]
  Suppressed = false
  Type = 0
FEATURE [Sketcher::SketchObject] Sketch021
  ArcFitTolerance = 1e-06
  AttachmentSupport = -> [XZ_Plane007]
  ExternalGeometry = -> [Revolution004]
  FullyConstrained = true
  MakeInternals = false
  MapMode = 5
  Placement = pos=(0,0,0) rot=(1,0,0;1.5708rad)
  sketch-geometry (2):
    g0: LineSegment [constr] StartX=-8.2 StartY=7 StartZ=0 EndX=0 EndY=7 EndZ=0
    g1: Circle CenterX=0 CenterY=7 CenterZ=0 NormalX=0 NormalY=0 NormalZ=1 AngleXU=0 Radius=1.5
  constraints (5):
    c: Symmetric(g-3,g-3,g0)
    c: PointOnObject(g0,g-2)
    c: Horizontal(g0)
    c: Coincident(g1,g0)
    c: Diameter(g1) = 3
FEATURE [PartDesign::Pocket] Pocket005
  BaseFeature = -> Revolution004
  Direction = (0,1,-2e-16)
  Length = 5
  Length2 = 5
  Midplane = true
  Placement = pos=(0,0,0) rot=(1,0,0;1.5708rad)
  Profile = -> Sketch021
  ReferenceAxis = -> Sketch021 [N_Axis]
  Suppressed = false
  Type = 1
FEATURE [PartDesign::Body] Body007  label="SwitchActuator"
  AllowCompound = false
  Group = -> [Sketch020,Revolution004,Sketch021,Pocket005]
  Origin = -> Origin007
  Tip = -> Pocket005
COMPONENT P8 — recipe-attached ("mountingPlate001", modeled in this document).
Construction recipe (the document's own serialized feature program — sketch geometry with constraints, then the solid features built on it; lengths are millimeters unless a unit is written):

FEATURE [Sketcher::SketchObject] Sketch
  ArcFitTolerance = 0
  AttachmentSupport = -> [XY_Plane]
  FullyConstrained = true
  MakeInternals = false
  MapMode = 5
  sketch-geometry (11):
    g0: LineSegment StartX=-12.7 StartY=8.1026 StartZ=0 EndX=-5.7589 EndY=18.8369 EndZ=0
    g1: ArcOfCircle CenterX=0 CenterY=15.113 CenterZ=0 NormalX=0 NormalY=0 NormalZ=1 AngleXU=0 Radius=6.858 StartAngle=0.574002 EndAngle=2.56759
    g2: LineSegment StartX=5.7589 StartY=18.8369 StartZ=0 EndX=12.7 EndY=8.1026 EndZ=0
    g3: LineSegment StartX=12.7 StartY=8.1026 StartZ=0 EndX=12.7 EndY=-8.1026 EndZ=0
    g4: LineSegment StartX=12.7 StartY=-8.1026 StartZ=0 EndX=5.7589 EndY=-18.8369 EndZ=0
    g5: ArcOfCircle CenterX=0 CenterY=-15.113 CenterZ=0 NormalX=0 NormalY=0 NormalZ=1 AngleXU=0 Radius=6.858 StartAngle=3.71559 EndAngle=5.70918
    g6: LineSegment StartX=-5.7589 StartY=-18.8369 StartZ=0 EndX=-12.7 EndY=-8.1026 EndZ=0
    g7: LineSegment StartX=-12.7 StartY=-8.1026 StartZ=0 EndX=-12.7 EndY=8.1026 EndZ=0
    g8: LineSegment [constr] StartX=0 StartY=21.971 StartZ=0 EndX=12.7 EndY=21.971 EndZ=0
    g9: Circle CenterX=2.5146 CenterY=-3.2766 CenterZ=0 NormalX=0 NormalY=0 NormalZ=1 AngleXU=0 Radius=5.5
    g10: LineSegment [constr] StartX=0 StartY=-21.971 StartZ=0 EndX=12.7 EndY=-21.971 EndZ=0
  constraints (30):
    c: Tangent(g0,g1) = 1.5708
    c: Tangent(g1,g2) = 1.5708
    c: Coincident(g2,g3)
    c: Coincident(g3,g4)
    c: Tangent(g4,g5) = 1.5708
    c: Tangent(g5,g6) = 1.5708
    c: Coincident(g6,g7)
    c: Coincident(g7,g0)
    c: Vertical(g7)
    c: PointOnObject(g1,g-2)
    c: Equal(g5,g1)
    c: PointOnObject(g8,g-2)
    c: Horizontal(g8)
    c: Vertical(g8,g2)
    c: Tangent(g8,g1)
    c: DistanceY(g8) = 21.971
    c: Symmetric(g1,g5,g-1)
    c: Symmetric(g0,g2,g-2)
    c: Equal(g7,g3)
    c: Symmetric(g3,g2,g-1)
    c: Radius(g5) = 6.858
    c: DistanceY(g2,g8) = 13.8684
    c: DistanceX(g6,g3) = 25.4
    c: DistanceX(g9,g3) = 10.1854
    c: Diameter(g9) = 11
    c: PointOnObject(g10,g-2)
    c: Horizontal(g10)
    c: Equal(g10,g8)
    c: Tangent(g10,g5)
    c: DistanceY(g10,g9) = 18.6944
FEATURE [PartDesign::Pad] Pad  label="BasePad"
  Direction = (0,0,1)
  Length = 3.17
  Length2 = 10
  Profile = -> Sketch
  ReferenceAxis = -> Sketch [N_Axis]
  Reversed = true
  Suppressed = false
  Type = 0
FEATURE [Sketcher::SketchObject] Sketch001
  ArcFitTolerance = 0
  AttachmentSupport = -> [XY_Plane]
  ExternalGeometry = -> [Pad]
  FullyConstrained = true
  MakeInternals = false
  MapMode = 5
  sketch-geometry (3):
    g0: Circle CenterX=0 CenterY=15.113 CenterZ=0 NormalX=0 NormalY=0 NormalZ=1 AngleXU=0 Radius=2.3114
    g1: Circle CenterX=0 CenterY=-15.113 CenterZ=0 NormalX=0 NormalY=0 NormalZ=1 AngleXU=0 Radius=2.3114
    g2: LineSegment [constr] StartX=0 StartY=21.971 StartZ=0 EndX=5.7589 EndY=21.971 EndZ=0
  constraints (9):
    c: PointOnObject(g0,g-2)
    c: Horizontal(g2)
    c: PointOnObject(g2,g-2)
    c: Vertical(g2,g-3)
    c: Tangent(g2,g-3)
    c: Equal(g0,g1)
    c: Diameter(g0) = 4.6228
    c: Symmetric(g0,g1,g-1)
    c: DistanceY(g0,g2) = 6.858
FEATURE [PartDesign::Hole] Hole
  BaseFeature = -> Pad
  CustomThreadClearance = 0
  Depth = 25
  DepthType = 0
  Diameter = 4.5
  DrillForDepth = false
  DrillPoint = 1
  DrillPointAngle = 118
  HoleCutCountersinkAngle = 90
  HoleCutCustomValues = false
  HoleCutDepth = 0
  HoleCutDiameter = 6.3
  HoleCutType = 2
  ModelThread = false
  Profile = -> Sketch001
  Suppressed = false
  Tapered = false
  TaperedAngle = 90
  ThreadClass = 0
  ThreadDepth = 25
  ThreadDepthType = 0
  ThreadDirection = 0
  ThreadFit = 0
  ThreadSize = 11
  ThreadType = 1
  Threaded = false
  UseCustomThreadClearance = false
FEATURE [PartDesign::Fillet] Fillet
  Base = -> Hole [Edge13,Edge14,Edge6,Edge3]
  BaseFeature = -> Hole
  Radius = 1
  SupportTransform = false
  Suppressed = false
  UseAllEdges = false
FEATURE [PartDesign::Body] Body  label="mountingPlate"
  AllowCompound = false
  Group = -> [Sketch,Pad,Sketch001,Hole,Fillet]
  Origin = -> Origin
  Tip = -> Fillet
PROVENANCE & LICENSES
A FreeCAD (.FCStd) document from a public repository crawl; recipes are the document's own serialized feature recipes (and, for linked parts, companion documents' recipes).
License: gpl-3.0.
